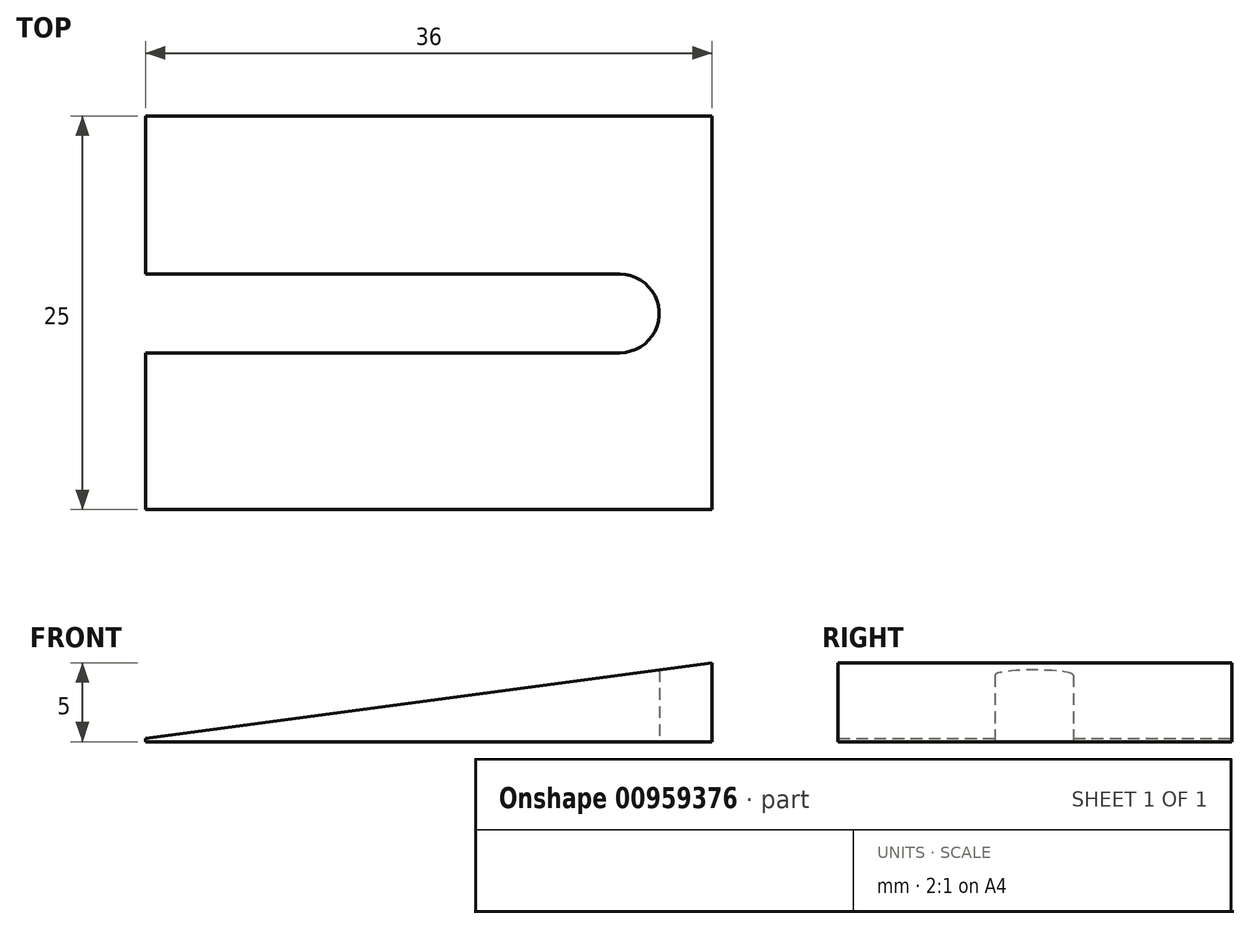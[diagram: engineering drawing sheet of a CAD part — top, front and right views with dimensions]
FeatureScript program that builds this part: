
annotation { "Feature Type Name" : "Feature", "Feature Type Description" : "" }
export const myFeature = defineFeature(function(context is Context, id is Id, definition is map)
    precondition{}
    {
        {
            var Q0;
            Q0=qCreatedBy(makeId("Front.planeOp"),FACE);
            var sketch = newSketch(context, id + "F0", { "sketchPlane" : qUnion([Q0])});
            skLineSegment(sketch, "E0", {"start": v(0, 0) * mm, "end": v(36, 0) * mm});
            skLineSegment(sketch, "E1", {"start": v(36, 0) * mm, "end": v(36, 5) * mm});
            skLineSegment(sketch, "E2", {"start": v(36, 5) * mm, "end": v(0, 0.2) * mm});
            skLineSegment(sketch, "E3", {"start": v(0, 0.2) * mm, "end": v(0, 0) * mm});
            skSolve(sketch);
        }
        {
            var Q0;
            Q0=makeQuery(id+"F0.imprint","IMPRINT",FACE,{"disambiguationData":[TD([[makeQuery(id+"F0.imprint","IMPRINT",EDGE,{"derivedFrom":sQuery(id+"F0.wireOp",EDGE,"E0")}),1.0]])]});
            extrude(context, id + "F1", {"entities" : qUnion([Q0]), "depth" : 25 * mm, "offsetDistance" : 25 * mm});
        }
        {
            var Q0;
            Q0=makeQuery(id+"F1.opExtrude","SWEPT_FACE",FACE,{"disambiguationData":[OSD([sQuery(id+"F0.wireOp",EDGE,"E0")])]});
            var sketch = newSketch(context, id + "F2", { "sketchPlane" : qUnion([Q0])});
            skCircle(sketch, "E4", {"center": v(30.15, 12.55) * mm, "radius": 2.5 * mm});
            skLineSegment(sketch, "E5", {"start": v(30.15, 10.05) * mm, "end": v(0, 10.05) * mm});
            skLineSegment(sketch, "E6", {"start": v(30.15, 15.05) * mm, "end": v(0, 15.05) * mm});
            skSolve(sketch);
        }
        {
            var Q0;
            Q0=sQuery(id+"F2.wireOp",VERTEX,"E4.center");
            var Q1;
            Q1=makeQuery(id+"F1.opExtrude","SWEPT_BODY",BODY,{"disambiguationData":[OSD([sQuery(id+"F0.wireOp",EDGE,"E0"),sQuery(id+"F0.wireOp",EDGE,"E1"),sQuery(id+"F0.wireOp",EDGE,"3qk3ftjO-Ehao-whPB-tabK-4CzWnRD2JLXx")])]});
            hole(context, id + "F3", {"style" : HoleStyle.SIMPLE, "endStyle" : HoleEndStyle.THROUGH, "holeDiameter" : 4 * mm, "majorDiameter" : 5 * mm, "isTappedThrough" : true, "tappedDepth" : 12 * mm, "tapClearance" : 3, "locations" : qUnion([Q0]), "scope" : qUnion([Q1])});
        }
        {
            var Q0;
            {var subQ0=sQuery(id+"F2.wireOp",EDGE,"E5");Q0=makeQuery(id+"F2.imprint","IMPRINT",FACE,{"disambiguationData":[TD([[makeQuery(id+"F2.imprint","IMPRINT",EDGE,{"derivedFrom":subQ0}),-1.0]])]});}
            var Q1;
            {var subQ0=sQuery(id+"F2.wireOp",EDGE,"E4");var subQ1=makeQuery(id+"F2.imprint","INTERSECT",VERTEX,{"derivedFrom":[subQ0,sQuery(id+"F2.wireOp",EDGE,"E5")]});Q1=makeQuery(id+"F2.imprint","IMPRINT",FACE,{"disambiguationData":[TD([[makeQuery(id+"F2.imprint","IMPRINT",EDGE,{"disambiguationData":[TD([[subQ1,1.0]])],"derivedFrom":subQ0}),1.0]])]});}
            extrude(context, id + "F4", {"entities" : qUnion([Q0, Q1]), "operationType" : NewBodyOperationType.REMOVE, "oppositeDirection" : true, "depth" : 25 * mm, "offsetDistance" : 25 * mm});
        }
    });
